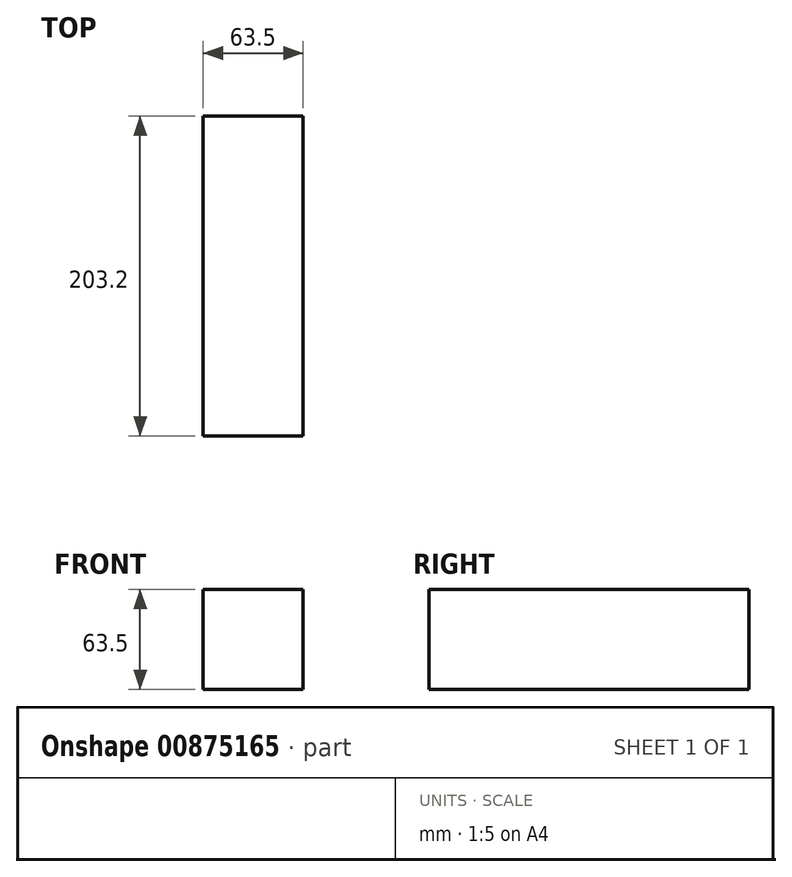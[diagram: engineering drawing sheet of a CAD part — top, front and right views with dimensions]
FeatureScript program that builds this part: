
annotation { "Feature Type Name" : "Feature", "Feature Type Description" : "" }
export const myFeature = defineFeature(function(context is Context, id is Id, definition is map)
    precondition{}
    {
        {
            var Q0;
            Q0=qCreatedBy(makeId("Front.planeOp"),FACE);
            var sketch = newSketch(context, id + "F0", { "sketchPlane" : qUnion([Q0])});
            skLineSegment(sketch, "E0.bottom", {"start": v(-164.57, 68.12) * mm, "end": v(-101.07, 68.12) * mm});
            skLineSegment(sketch, "E0.top", {"start": v(-164.57, 4.62) * mm, "end": v(-101.07, 4.62) * mm});
            skLineSegment(sketch, "E0.left", {"start": v(-164.57, 68.12) * mm, "end": v(-164.57, 4.62) * mm});
            skLineSegment(sketch, "E0.right", {"start": v(-101.07, 68.12) * mm, "end": v(-101.07, 4.62) * mm});
            skSolve(sketch);
        }
        {
            var Q0;
            Q0=makeQuery(id+"F0.imprint","IMPRINT",FACE,{"disambiguationData":[TD([[makeQuery(id+"F0.imprint","IMPRINT",EDGE,{"derivedFrom":sQuery(id+"F0.wireOp",EDGE,"E0.bottom")}),-1.0]])]});
            extrude(context, id + "F1", {"entities" : qUnion([Q0]), "depth" : 1498.6 * mm, "offsetDistance" : 25.4 * mm});
        }
        {
            var Q0;
            Q0=makeQuery(id+"F1.opExtrude","CAP_FACE",FACE,{"disambiguationData":[OSD([sQuery(id+"F0.wireOp",EDGE,"E0.bottom"),sQuery(id+"F0.wireOp",EDGE,"E0.top"),sQuery(id+"F0.wireOp",EDGE,"E0.left"),sQuery(id+"F0.wireOp",EDGE,"E0.right")])],"isStart":true});
            extrude(context, id + "F2", {"entities" : qUnion([Q0]), "operationType" : NewBodyOperationType.REMOVE, "oppositeDirection" : true, "depth" : 1092.2 * mm, "offsetDistance" : 25.4 * mm});
        }
        {
            var Q0;
            Q0=makeQuery(id+"F2.boolean.opBoolean","COPY",FACE,{"derivedFrom":makeQuery(id+"F2.opExtrude","CAP_FACE",FACE,{"disambiguationData":[OSD([sQuery(id+"F0.wireOp",EDGE,"E0.bottom"),sQuery(id+"F0.wireOp",EDGE,"E0.top"),sQuery(id+"F0.wireOp",EDGE,"E0.left"),sQuery(id+"F0.wireOp",EDGE,"E0.right")])],"isStart":false})});
            extrude(context, id + "F3", {"entities" : qUnion([Q0]), "operationType" : NewBodyOperationType.REMOVE, "oppositeDirection" : true, "depth" : 203.2 * mm, "offsetDistance" : 25.4 * mm});
        }
    });
